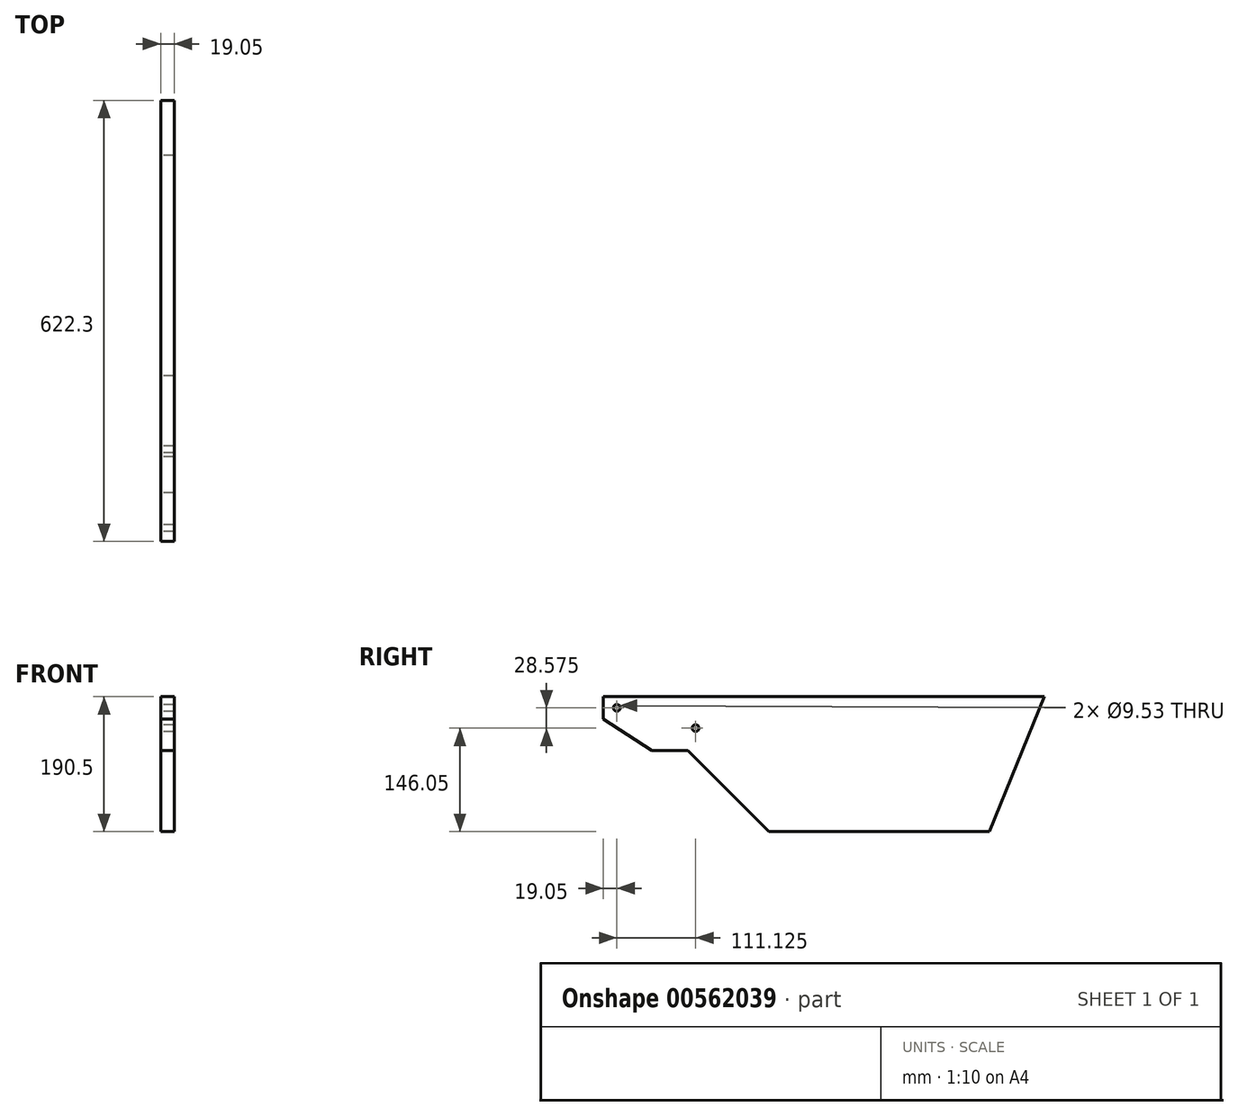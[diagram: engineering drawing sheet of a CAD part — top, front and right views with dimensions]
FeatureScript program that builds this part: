
annotation { "Feature Type Name" : "Feature", "Feature Type Description" : "" }
export const myFeature = defineFeature(function(context is Context, id is Id, definition is map)
    precondition{}
    {
        {
            var Q0;
            Q0=qCreatedBy(makeId("Right.planeOp"),FACE);
            var sketch = newSketch(context, id + "F0", { "sketchPlane" : qUnion([Q0])});
            skLineSegment(sketch, "E0", {"start": v(-513.86, 319.86) * mm, "end": v(-513.86, 78.56) * mm});
            skSolve(sketch);
        }
        {
            var Q0;
            Q0=qCreatedBy(makeId("Right.planeOp"),FACE);
            var sketch = newSketch(context, id + "F1", { "sketchPlane" : qUnion([Q0])});
            skLineSegment(sketch, "E1", {"start": v(-749.76, 256.37) * mm, "end": v(-601.81, 261.03) * mm});
            skLineSegment(sketch, "E2", {"start": v(-560.54, 653.66) * mm, "end": v(-601.81, 261.03) * mm});
            skLineSegment(sketch, "E3", {"start": v(-560.54, 653.66) * mm, "end": v(-749.76, 256.37) * mm});
            skLineSegment(sketch, "E4", {"start": v(-712.77, 291.22) * mm, "end": v(-723.7, 436.42) * mm});
            skLineSegment(sketch, "E5", {"start": v(-712.77, 291.22) * mm, "end": v(-826.16, 542.64) * mm});
            skLineSegment(sketch, "E6", {"start": v(-723.7, 436.42) * mm, "end": v(-826.16, 542.64) * mm});
            skLineSegment(sketch, "E7", {"start": v(-1007.93, 660.27) * mm, "end": v(-826.16, 542.64) * mm});
            skLineSegment(sketch, "E8", {"start": v(-1037.12, 677.37) * mm, "end": v(-1007.93, 660.27) * mm});
            skLineSegment(sketch, "E9", {"start": v(-1037.12, 677.37) * mm, "end": v(-712.77, 291.22) * mm});
            skLineSegment(sketch, "E10", {"start": v(-1007.93, 660.27) * mm, "end": v(-712.77, 291.22) * mm});
            skLineSegment(sketch, "E11", {"start": v(-601.81, 261.03) * mm, "end": v(-595.01, 401.75) * mm});
            skLineSegment(sketch, "E12", {"start": v(-601.81, 261.03) * mm, "end": v(-607.25, 655.88) * mm});
            skLineSegment(sketch, "E13", {"start": v(-595.01, 401.75) * mm, "end": v(-607.25, 655.88) * mm});
            skLineSegment(sketch, "E14", {"start": v(-723.7, 436.42) * mm, "end": v(-595.01, 401.75) * mm});
            skLineSegment(sketch, "E15", {"start": v(-826.16, 542.64) * mm, "end": v(-774.61, 590.25) * mm});
            skLineSegment(sketch, "E16", {"start": v(-749.76, 256.37) * mm, "end": v(-774.61, 590.25) * mm});
            skLineSegment(sketch, "E17", {"start": v(-1041.29, 793.41) * mm, "end": v(-774.61, 590.25) * mm});
            skLineSegment(sketch, "E18", {"start": v(-1390.78, 317.95) * mm, "end": v(-1336.8, 360.93) * mm});
            skLineSegment(sketch, "E19", {"start": v(-1336.8, 360.93) * mm, "end": v(-1295.1, 301.57) * mm});
            skLineSegment(sketch, "E20", {"start": v(-1041.29, 793.41) * mm, "end": v(-1295.1, 301.57) * mm});
            skLineSegment(sketch, "E21", {"start": v(-1295.1, 301.57) * mm, "end": v(-1037.12, 677.37) * mm});
            skLineSegment(sketch, "E22", {"start": v(-1037.12, 677.37) * mm, "end": v(-1041.29, 793.41) * mm});
            skLineSegment(sketch, "E23", {"start": v(-1007.93, 660.27) * mm, "end": v(-1336.8, 360.93) * mm});
            skLineSegment(sketch, "E24", {"start": v(-1390.78, 317.95) * mm, "end": v(-1295.1, 301.57) * mm});
            skLineSegment(sketch, "E25", {"start": v(-1295.1, 301.57) * mm, "end": v(-1295.1, 192.57) * mm});
            skLineSegment(sketch, "E26", {"start": v(-1295.1, 192.57) * mm, "end": v(-1403.22, 211.07) * mm});
            skLineSegment(sketch, "E27", {"start": v(-1403.22, 211.07) * mm, "end": v(-1390.78, 317.95) * mm});
            skLineSegment(sketch, "E28", {"start": v(-1390.78, 317.95) * mm, "end": v(-1295.1, 192.57) * mm});
            skLineSegment(sketch, "E29", {"start": v(0, 0) * mm, "end": v(0, 674.17) * mm});
            skLineSegment(sketch, "E30", {"start": v(-316.61, 320.6) * mm, "end": v(-316.61, 307.94) * mm});
            skLineSegment(sketch, "E31", {"start": v(-400.45, 218.07) * mm, "end": v(-378.01, 218.07) * mm});
            skLineSegment(sketch, "E32", {"start": v(-472.6, 74.76) * mm, "end": v(-472.6, 54.94) * mm});
            skSolve(sketch);
        }
        {
            var Q0;
            Q0=qCreatedBy(makeId("Right.planeOp"),FACE);
            var sketch = newSketch(context, id + "F2", { "sketchPlane" : qUnion([Q0])});
            skLineSegment(sketch, "E33", {"start": v(-497.84, 114.3) * mm, "end": v(-186.7, 114.3) * mm});
            skLineSegment(sketch, "E34", {"start": v(-186.7, 114.3) * mm, "end": v(-109.22, 304.8) * mm});
            skLineSegment(sketch, "E35", {"start": v(-109.22, 304.8) * mm, "end": v(-731.52, 304.8) * mm});
            skLineSegment(sketch, "E36", {"start": v(-662.94, 228.6) * mm, "end": v(-612.14, 228.6) * mm});
            skLineSegment(sketch, "E37", {"start": v(-612.14, 228.6) * mm, "end": v(-497.84, 114.3) * mm});
            skLineSegment(sketch, "E38", {"start": v(-731.52, 304.8) * mm, "end": v(-731.52, 273.05) * mm});
            skLineSegment(sketch, "E39", {"start": v(-731.52, 273.05) * mm, "end": v(-662.94, 228.6) * mm});
            skCircle(sketch, "E40", {"center": v(-712.47, 288.92) * mm, "radius": 4.76 * mm});
            skCircle(sketch, "E41", {"center": v(-601.35, 260.35) * mm, "radius": 4.76 * mm});
            skSolve(sketch);
        }
        {
            var Q0;
            Q0 = qSketchRegion(id + "F2", true);
            extrude(context, id + "F3", {"entities" : qUnion([Q0]), "depth" : 19.05 * mm, "offsetDistance" : 25.4 * mm});
        }
    });
